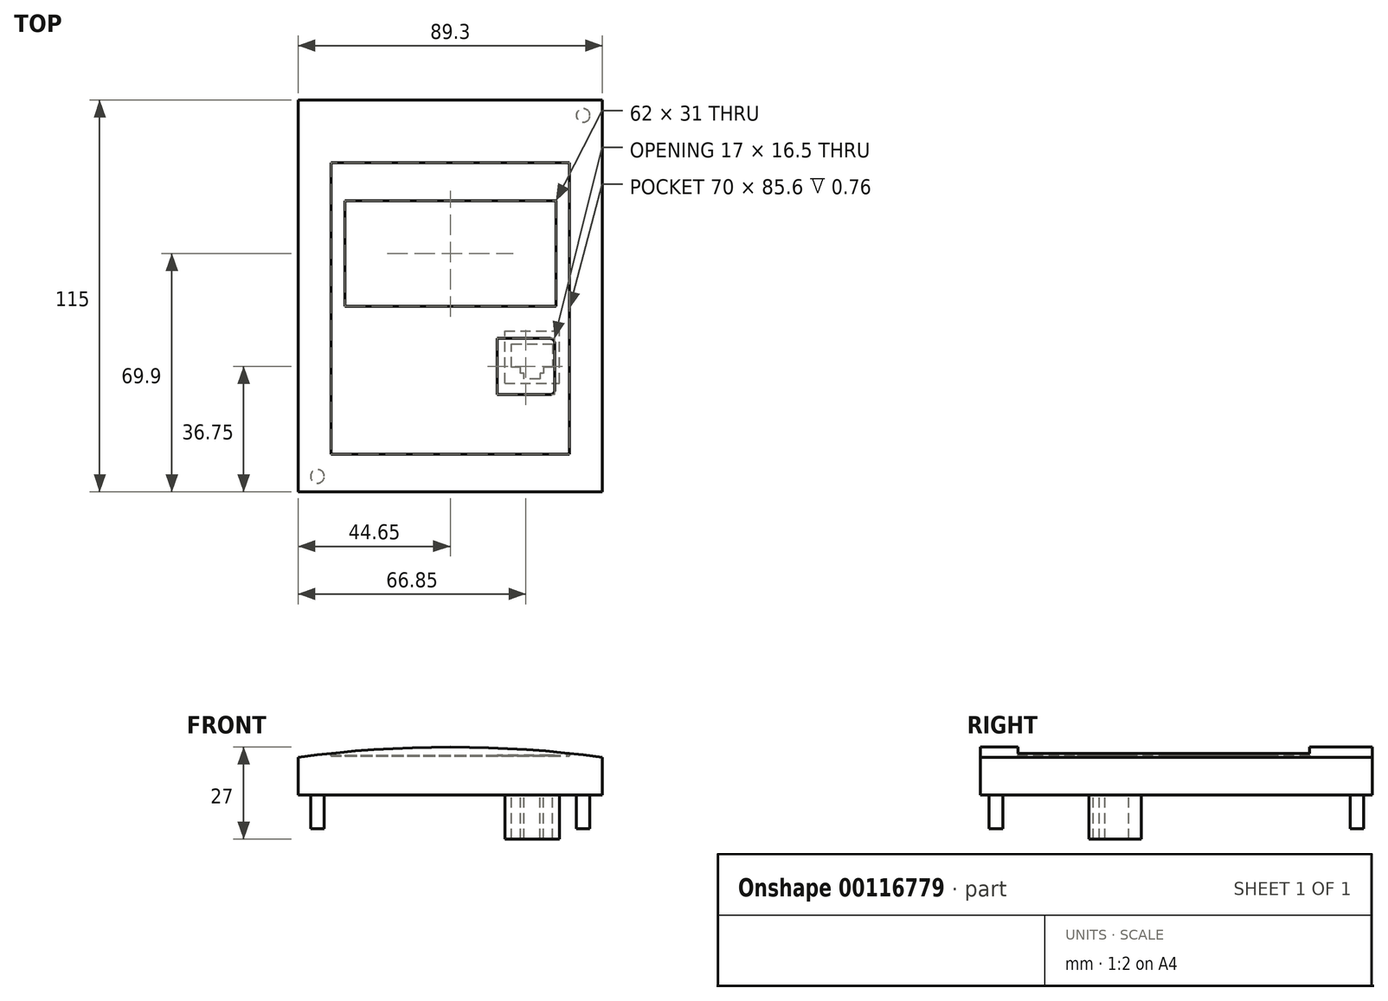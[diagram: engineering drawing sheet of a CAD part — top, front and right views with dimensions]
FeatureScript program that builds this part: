
annotation { "Feature Type Name" : "Feature", "Feature Type Description" : "" }
export const myFeature = defineFeature(function(context is Context, id is Id, definition is map)
    precondition{}
    {
        {
            var Q0;
            Q0=qCreatedBy(makeId("Front.planeOp"),FACE);
            var sketch = newSketch(context, id + "F0", { "sketchPlane" : qUnion([Q0])});
            skLineSegment(sketch, "E0", {"start": v(0, 0) * mm, "end": v(-44.65, 0) * mm});
            skLineSegment(sketch, "E1", {"start": v(-44.65, 0) * mm, "end": v(-44.65, 21) * mm});
            skLineSegment(sketch, "E2", {"start": v(0, 0) * mm, "end": v(0, 24) * mm});
            skLineSegment(sketch, "E3", {"start": v(0, 0) * mm, "end": v(44.65, 0) * mm});
            skLineSegment(sketch, "E4", {"start": v(44.65, 0) * mm, "end": v(44.65, 21) * mm});
            skArc(sketch, "E5", {"start": v(44.65, 21) * mm, "mid": v(0, 24) * mm, "end": v(-44.65, 21) * mm});
            skSolve(sketch);
        }
        {
            var Q0;
            Q0=makeQuery(id+"F0.imprint","IMPRINT",FACE,{"disambiguationData":[TD([[makeQuery(id+"F0.imprint","IMPRINT",EDGE,{"derivedFrom":sQuery(id+"F0.wireOp",EDGE,"E0")}),-1.0]])]});
            var Q1;
            {var subQ0=sQuery(id+"F0.wireOp",EDGE,"E2");Q1=makeQuery(id+"F0.imprint","IMPRINT",FACE,{"disambiguationData":[TD([[makeQuery(id+"F0.imprint","IMPRINT",EDGE,{"derivedFrom":subQ0}),-1.0]])]});}
            extrude(context, id + "F1", {"entities" : qUnion([Q0, Q1]), "endBound" : BoundingType.SYMMETRIC, "depth" : 115 * mm});
        }
        {
            var Q0;
            Q0=makeQuery(id+"F1.opExtrude","SWEPT_FACE",FACE,{"disambiguationData":[OSD([sQuery(id+"F0.wireOp",EDGE,"E0"),sQuery(id+"F0.wireOp",EDGE,"E3")])]});
            var sketch = newSketch(context, id + "F2", { "sketchPlane" : qUnion([Q0])});
            skCircle(sketch, "E6", {"center": v(-39, -53) * mm, "radius": 2 * mm});
            skCircle(sketch, "E7.MirrorC", {"center": v(-39, 53) * mm, "radius": 2 * mm});
            skCircle(sketch, "E8.MirrorC", {"center": v(39, 53) * mm, "radius": 2 * mm});
            skCircle(sketch, "E9.MirrorC", {"center": v(39, -53) * mm, "radius": 2 * mm});
            skLineSegment(sketch, "E10.bottom", {"start": v(16, 25.65) * mm, "end": v(32, 25.65) * mm});
            skLineSegment(sketch, "E10.top", {"start": v(16, 10.35) * mm, "end": v(32, 10.35) * mm});
            skLineSegment(sketch, "E10.left", {"start": v(16, 25.65) * mm, "end": v(16, 10.35) * mm});
            skLineSegment(sketch, "E10.right", {"start": v(32, 25.65) * mm, "end": v(32, 10.35) * mm});
            skPoint(sketch, "E11", {"position": v(32, 18) * mm});
            skPoint(sketch, "E12", {"position": v(24, 10.35) * mm});
            skLineSegment(sketch, "E13", {"start": v(17.95, 14.05) * mm, "end": v(30.05, 14.05) * mm});
            skLineSegment(sketch, "E14", {"start": v(30.05, 14.05) * mm, "end": v(30.05, 20.95) * mm});
            skLineSegment(sketch, "E15", {"start": v(30.05, 20.95) * mm, "end": v(27.35, 20.95) * mm});
            skLineSegment(sketch, "E16", {"start": v(27.35, 20.95) * mm, "end": v(27.35, 22.7) * mm});
            skLineSegment(sketch, "E17", {"start": v(27.35, 22.7) * mm, "end": v(26.3, 22.7) * mm});
            skLineSegment(sketch, "E18", {"start": v(26.3, 22.7) * mm, "end": v(26.3, 24.45) * mm});
            skLineSegment(sketch, "E19", {"start": v(26.3, 24.45) * mm, "end": v(21.7, 24.45) * mm});
            skLineSegment(sketch, "E20", {"start": v(21.7, 24.45) * mm, "end": v(21.7, 22.7) * mm});
            skLineSegment(sketch, "E21", {"start": v(21.7, 22.7) * mm, "end": v(20.65, 22.7) * mm});
            skLineSegment(sketch, "E22", {"start": v(20.65, 22.7) * mm, "end": v(20.65, 20.95) * mm});
            skLineSegment(sketch, "E23", {"start": v(20.65, 20.95) * mm, "end": v(17.95, 20.95) * mm});
            skLineSegment(sketch, "E24", {"start": v(17.95, 20.95) * mm, "end": v(17.95, 14.05) * mm});
            skPoint(sketch, "E25", {"position": v(24, 14.05) * mm});
            skSolve(sketch);
        }
        {
            var Q0;
            Q0=makeQuery(id+"F2.imprint","IMPRINT",FACE,{"disambiguationData":[TD([[makeQuery(id+"F2.imprint","IMPRINT",EDGE,{"derivedFrom":sQuery(id+"F2.wireOp",EDGE,"E10.bottom")}),-1.0]])]});
            extrude(context, id + "F3", {"entities" : qUnion([Q0]), "operationType" : NewBodyOperationType.ADD, "depth" : 3 * mm});
        }
        {
            var Q0;
            Q0=makeQuery(id+"F2.imprint","IMPRINT",FACE,{"disambiguationData":[TD([[makeQuery(id+"F2.imprint","IMPRINT",EDGE,{"derivedFrom":sQuery(id+"F2.wireOp",EDGE,"E13")}),1.0]])]});
            var Q1;
            Q1=makeQuery(id+"F2.imprint","IMPRINT",FACE,{"disambiguationData":[TD([[makeQuery(id+"F2.imprint","IMPRINT",EDGE,{"derivedFrom":sQuery(id+"F2.wireOp",EDGE,"E8.MirrorC")}),1.0]])]});
            var Q2;
            Q2=makeQuery(id+"F2.imprint","IMPRINT",FACE,{"disambiguationData":[TD([[makeQuery(id+"F2.imprint","IMPRINT",EDGE,{"derivedFrom":sQuery(id+"F2.wireOp",EDGE,"E7.MirrorC")}),-1.0]])]});
            var Q3;
            Q3=makeQuery(id+"F2.imprint","IMPRINT",FACE,{"disambiguationData":[TD([[makeQuery(id+"F2.imprint","IMPRINT",EDGE,{"derivedFrom":sQuery(id+"F2.wireOp",EDGE,"E6")}),1.0]])]});
            var Q4;
            Q4=makeQuery(id+"F2.imprint","IMPRINT",FACE,{"disambiguationData":[TD([[makeQuery(id+"F2.imprint","IMPRINT",EDGE,{"derivedFrom":sQuery(id+"F2.wireOp",EDGE,"E9.MirrorC")}),-1.0]])]});
            extrude(context, id + "F4", {"entities" : qUnion([Q0, Q1, Q2, Q3, Q4]), "operationType" : NewBodyOperationType.REMOVE, "oppositeDirection" : true, "depth" : 10 * mm});
        }
        {
            var Q0;
            Q0=qCreatedBy(makeId("Top.planeOp"),FACE);
            cPlane(context, id + "F5", {"entities" : qUnion([Q0]), "cplaneType" : CPlaneType.OFFSET, "offset" : 24 * mm, "width" : 150 * mm, "height" : 150 * mm});
        }
        {
            var Q0;
            Q0=qCreatedBy(id+"F5.planeOp",FACE);
            var sketch = newSketch(context, id + "F6", { "sketchPlane" : qUnion([Q0])});
            skLineSegment(sketch, "E26.bottom", {"start": v(-35, 39.1) * mm, "end": v(35, 39.1) * mm});
            skLineSegment(sketch, "E26.top", {"start": v(-35, -46.5) * mm, "end": v(35, -46.5) * mm});
            skLineSegment(sketch, "E26.left", {"start": v(-35, 39.1) * mm, "end": v(-35, -46.5) * mm});
            skLineSegment(sketch, "E26.right", {"start": v(35, 39.1) * mm, "end": v(35, -46.5) * mm});
            skPoint(sketch, "E27", {"position": v(0, 39.1) * mm});
            skPoint(sketch, "E28", {"position": v(35, -3.7) * mm});
            skSolve(sketch);
        }
        {
            var Q0;
            Q0=makeQuery(id+"F6.imprint","IMPRINT",FACE,{"disambiguationData":[TD([[makeQuery(id+"F6.imprint","IMPRINT",EDGE,{"derivedFrom":sQuery(id+"F6.wireOp",EDGE,"E26.bottom")}),-1.0]])]});
            extrude(context, id + "F7", {"entities" : qUnion([Q0]), "operationType" : NewBodyOperationType.REMOVE, "oppositeDirection" : true, "depth" : 2.6 * mm});
        }
        {
            var Q0;
            Q0=makeQuery(id+"F7.boolean.opBoolean","COPY",FACE,{"derivedFrom":makeQuery(id+"F7.opExtrude","CAP_FACE",FACE,{"disambiguationData":[OSD([sQuery(id+"F6.wireOp",EDGE,"E26.bottom"),sQuery(id+"F6.wireOp",EDGE,"E26.top"),sQuery(id+"F6.wireOp",EDGE,"E26.left"),sQuery(id+"F6.wireOp",EDGE,"E26.right")])],"isStart":false})});
            var sketch = newSketch(context, id + "F8", { "sketchPlane" : qUnion([Q0])});
            skLineSegment(sketch, "E29.bottom", {"start": v(-31, 27.9) * mm, "end": v(31, 27.9) * mm});
            skLineSegment(sketch, "E29.top", {"start": v(-31, -3.1) * mm, "end": v(31, -3.1) * mm});
            skLineSegment(sketch, "E29.left", {"start": v(-31, 27.9) * mm, "end": v(-31, -3.1) * mm});
            skLineSegment(sketch, "E29.right", {"start": v(31, 27.9) * mm, "end": v(31, -3.1) * mm});
            skPoint(sketch, "E30", {"position": v(0, -3.1) * mm});
            skLineSegment(sketch, "E31.bottom", {"start": v(-29.2, -12.5) * mm, "end": v(-13.7, -12.5) * mm});
            skLineSegment(sketch, "E31.top", {"start": v(-29.2, -29) * mm, "end": v(-13.7, -29) * mm});
            skLineSegment(sketch, "E31.left", {"start": v(-30.7, -14) * mm, "end": v(-30.7, -27.5) * mm});
            skLineSegment(sketch, "E31.right", {"start": v(-13.7, -12.5) * mm, "end": v(-13.7, -29) * mm});
            skPoint(sketch, "E32.visualSharp", {"position": v(-30.7, -12.5) * mm});
            skArc(sketch, "E32.filletArc", {"start": v(-29.2, -12.5) * mm, "mid": v(-30.26, -12.94) * mm, "end": v(-30.7, -14) * mm});
            skPoint(sketch, "E33.visualSharp", {"position": v(-30.7, -29) * mm});
            skArc(sketch, "E33.filletArc", {"start": v(-30.7, -27.5) * mm, "mid": v(-30.26, -28.56) * mm, "end": v(-29.2, -29) * mm});
            skArc(sketch, "E34.MirrorCS", {"start": v(30.7, -27.5) * mm, "mid": v(30.26, -28.56) * mm, "end": v(29.2, -29) * mm});
            skArc(sketch, "E35.MirrorCS", {"start": v(29.2, -12.5) * mm, "mid": v(30.26, -12.94) * mm, "end": v(30.7, -14) * mm});
            skPoint(sketch, "E36.MirrorP", {"position": v(30.7, -12.5) * mm});
            skLineSegment(sketch, "E37.MirrorCS", {"start": v(29.2, -12.5) * mm, "end": v(13.7, -12.5) * mm});
            skPoint(sketch, "E38.MirrorP", {"position": v(30.7, -29) * mm});
            skLineSegment(sketch, "E39.MirrorCS", {"start": v(29.2, -29) * mm, "end": v(13.7, -29) * mm});
            skLineSegment(sketch, "E40.MirrorCS", {"start": v(30.7, -14) * mm, "end": v(30.7, -27.5) * mm});
            skLineSegment(sketch, "E41.MirrorCS", {"start": v(13.7, -12.5) * mm, "end": v(13.7, -29) * mm});
            skLineSegment(sketch, "E42", {"start": v(-10.65, -9.75) * mm, "end": v(-10.65, -31.75) * mm});
            skPoint(sketch, "E43", {"position": v(-13.7, -20.75) * mm});
            skPoint(sketch, "E44", {"position": v(-10.65, -20.75) * mm});
            skLineSegment(sketch, "E45", {"start": v(10.65, -9.75) * mm, "end": v(10.65, -31.75) * mm});
            skArc(sketch, "E46", {"start": v(10.65, -9.75) * mm, "mid": v(0, -8.3) * mm, "end": v(-10.65, -9.75) * mm});
            skArc(sketch, "E47", {"start": v(-10.65, -31.75) * mm, "mid": v(0, -33.2) * mm, "end": v(10.65, -31.75) * mm});
            skSolve(sketch);
        }
        {
            var Q0;
            Q0=makeQuery(id+"F8.imprint","IMPRINT",FACE,{"disambiguationData":[TD([[makeQuery(id+"F8.imprint","IMPRINT",EDGE,{"derivedFrom":sQuery(id+"F8.wireOp",EDGE,"E29.bottom")}),-1.0]])]});
            extrude(context, id + "F9", {"entities" : qUnion([Q0]), "depth" : 0.1 * mm});
        }
        {
            var Q0;
            Q0=makeQuery(id+"F8.imprint","IMPRINT",FACE,{"disambiguationData":[TD([[makeQuery(id+"F8.imprint","IMPRINT",EDGE,{"derivedFrom":sQuery(id+"F8.wireOp",EDGE,"E31.bottom")}),-1.0]])]});
            var Q1;
            Q1=makeQuery(id+"F8.imprint","IMPRINT",FACE,{"disambiguationData":[TD([[makeQuery(id+"F8.imprint","IMPRINT",EDGE,{"derivedFrom":sQuery(id+"F8.wireOp",EDGE,"E34.MirrorCS")}),-1.0]])]});
            var Q2;
            Q2=makeQuery(id+"F8.imprint","IMPRINT",FACE,{"disambiguationData":[TD([[makeQuery(id+"F8.imprint","IMPRINT",EDGE,{"derivedFrom":sQuery(id+"F8.wireOp",EDGE,"E42")}),1.0]])]});
            extrude(context, id + "F10", {"entities" : qUnion([Q0, Q1, Q2]), "depth" : 0.2 * mm});
        }
    });
